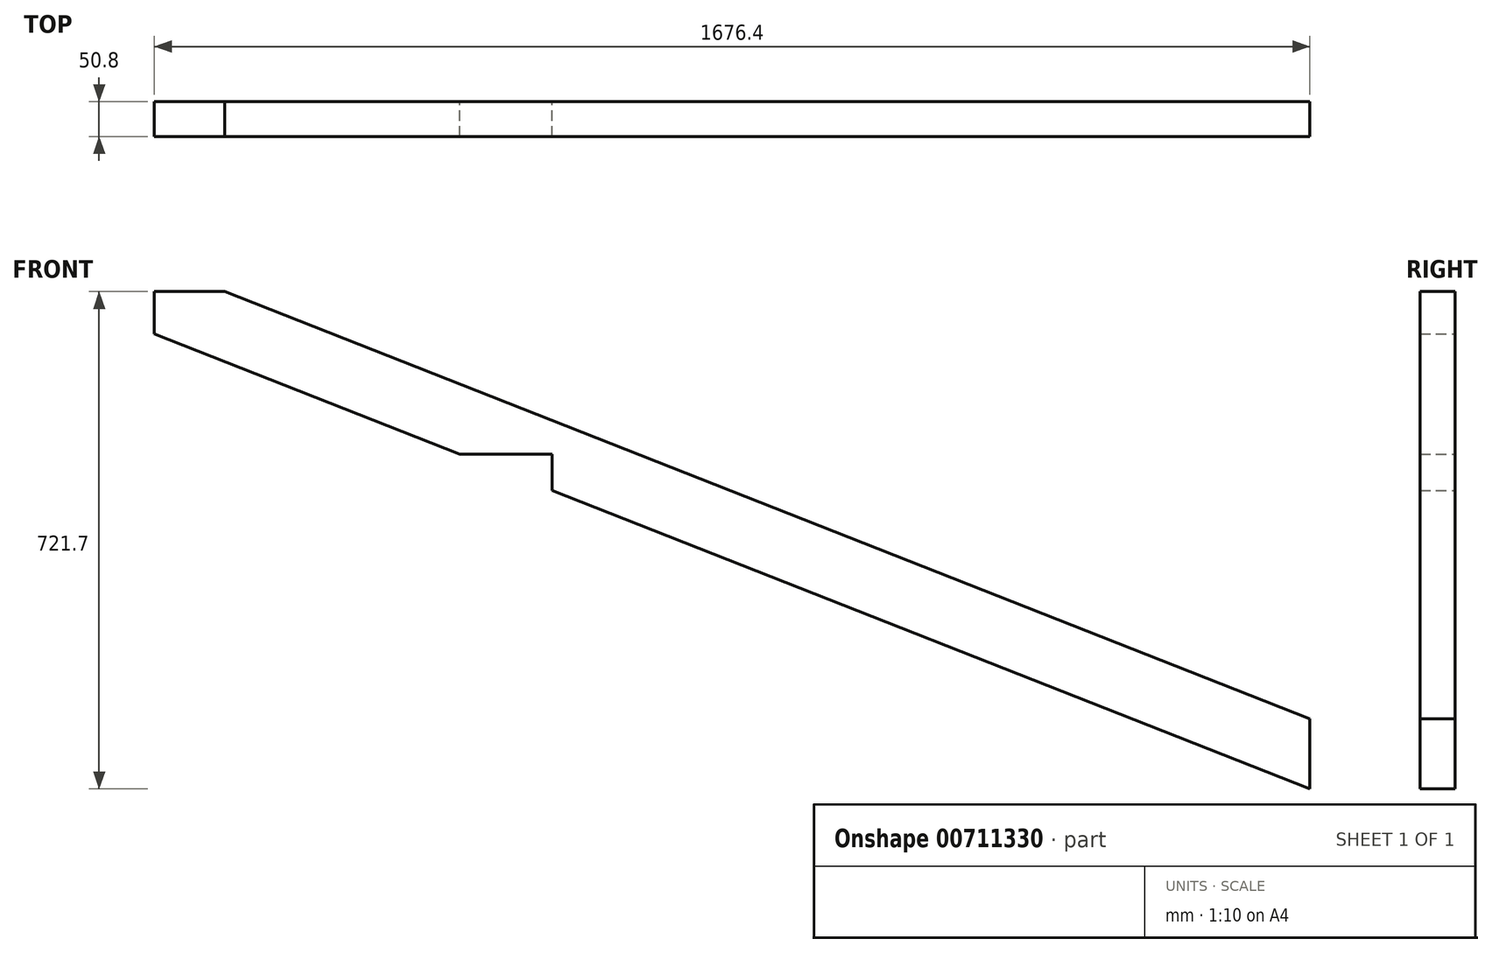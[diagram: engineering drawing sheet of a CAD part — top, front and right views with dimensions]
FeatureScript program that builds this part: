
annotation { "Feature Type Name" : "Feature", "Feature Type Description" : "" }
export const myFeature = defineFeature(function(context is Context, id is Id, definition is map)
    precondition{}
    {
        {
            var Q0;
            Q0=qCreatedBy(makeId("Front.planeOp"),FACE);
            var sketch = newSketch(context, id + "F0", { "sketchPlane" : qUnion([Q0])});
            skLineSegment(sketch, "E0", {"start": v(868.11, 332.86) * mm, "end": v(868.11, 394.16) * mm});
            skLineSegment(sketch, "E1.MirrorCS", {"start": v(868.11, 332.86) * mm, "end": v(1310.95, 158.4) * mm});
            skLineSegment(sketch, "E2.MirrorCS", {"start": v(2544.51, -327.54) * mm, "end": v(2544.51, -225.94) * mm});
            skLineSegment(sketch, "E3.MirrorCS", {"start": v(970.4, 394.16) * mm, "end": v(2544.51, -225.94) * mm});
            skPoint(sketch, "E4.end.orphan", {"position": v(-808.29, -225.94) * mm});
            skPoint(sketch, "E4.start.orphan", {"position": v(-808.29, -327.54) * mm});
            skPoint(sketch, "E5.end.orphan", {"position": v(868.11, -327.54) * mm});
            skLineSegment(sketch, "E6.bottom", {"start": v(1310.95, 158.4) * mm, "end": v(1445.06, 158.4) * mm});
            skLineSegment(sketch, "E6.right", {"start": v(1445.06, 158.4) * mm, "end": v(1445.06, 105.57) * mm});
            skPoint(sketch, "E6.middle", {"position": v(1378, 131.99) * mm});
            skPoint(sketch, "E6.top.start.orphan", {"position": v(1310.95, 105.57) * mm});
            skLineSegment(sketch, "E7.trimOffspring", {"start": v(1445.06, 105.57) * mm, "end": v(2544.51, -327.54) * mm});
            skPoint(sketch, "E8.orphan", {"position": v(868.11, 434.46) * mm});
            skLineSegment(sketch, "E9", {"start": v(970.4, 394.16) * mm, "end": v(868.11, 394.16) * mm});
            skSolve(sketch);
        }
        {
            var Q0;
            Q0=makeQuery(id+"F0.imprint","IMPRINT",FACE,{"disambiguationData":[TD([[makeQuery(id+"F0.imprint","IMPRINT",EDGE,{"derivedFrom":sQuery(id+"F0.wireOp",EDGE,"E0")}),-1.0]])]});
            extrude(context, id + "F1", {"entities" : qUnion([Q0]), "depth" : 50.8 * mm, "offsetDistance" : 25.4 * mm});
        }
    });
